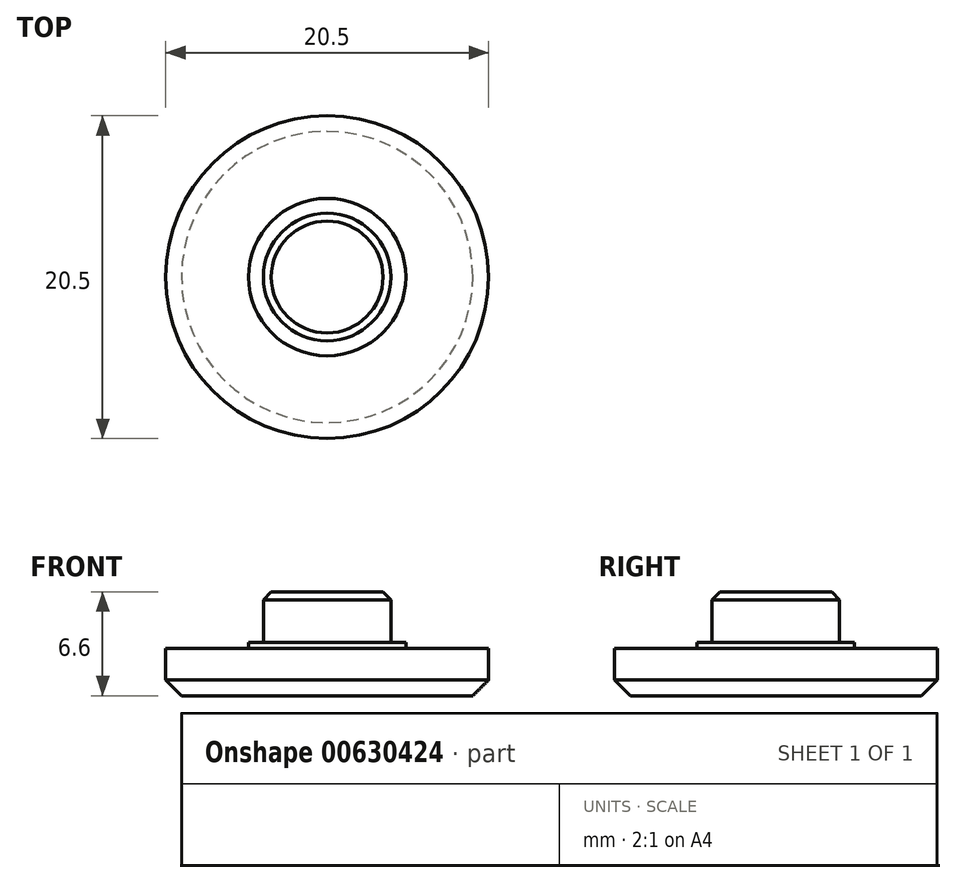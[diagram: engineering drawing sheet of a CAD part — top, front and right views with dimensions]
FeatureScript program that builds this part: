
annotation { "Feature Type Name" : "Feature", "Feature Type Description" : "" }
export const myFeature = defineFeature(function(context is Context, id is Id, definition is map)
    precondition{}
    {
        {
            var Q0;
            Q0=qCreatedBy(makeId("Top.planeOp"),FACE);
            var sketch = newSketch(context, id + "F0", { "sketchPlane" : qUnion([Q0])});
            skCircle(sketch, "E0", {"center": v(0, 0) * mm, "radius": 4.05 * mm});
            skCircle(sketch, "E1", {"center": v(0, 0) * mm, "radius": 10.25 * mm});
            skCircle(sketch, "E2", {"center": v(0, 0) * mm, "radius": 5 * mm});
            skSolve(sketch);
        }
        {
            assignVariable(context, id + "F1", {"name" : "CapThickness", "anyValue" : 3});
        }
        {
            assignVariable(context, id + "F2", {"name" : "Flange", "anyValue" : 0.4});
        }
        {
            assignVariable(context, id + "F3", {"name" : "Insert", "anyValue" : 3.2});
        }
        {
            var Q0;
            Q0=makeQuery(id+"F0.imprint","IMPRINT",FACE,{"disambiguationData":[TD([[makeQuery(id+"F0.imprint","IMPRINT",EDGE,{"derivedFrom":sQuery(id+"F0.wireOp",EDGE,"E1")}),1.0]])]});
            extrude(context, id + "F4", {"entities" : qUnion([Q0]), "depth" : (getVariable(context, 'CapThickness')) * mm, "offsetDistance" : 25 * mm});
        }
        {
            var Q0;
            Q0=makeQuery(id+"F0.imprint","IMPRINT",FACE,{"disambiguationData":[TD([[makeQuery(id+"F0.imprint","IMPRINT",EDGE,{"derivedFrom":sQuery(id+"F0.wireOp",EDGE,"E0")}),-1.0]])]});
            extrude(context, id + "F5", {"entities" : qUnion([Q0]), "operationType" : NewBodyOperationType.ADD, "depth" : (getVariable(context, 'CapThickness') + getVariable(context, 'Flange')) * mm, "offsetDistance" : 25 * mm});
        }
        {
            var Q0;
            Q0=makeQuery(id+"F0.imprint","IMPRINT",FACE,{"disambiguationData":[TD([[makeQuery(id+"F0.imprint","IMPRINT",EDGE,{"derivedFrom":sQuery(id+"F0.wireOp",EDGE,"E0")}),1.0]])]});
            extrude(context, id + "F6", {"entities" : qUnion([Q0]), "operationType" : NewBodyOperationType.ADD, "depth" : (getVariable(context, 'CapThickness') + getVariable(context, 'Flange') + getVariable(context, 'Insert')) * mm, "offsetDistance" : 25 * mm});
        }
        {
            var Q0;
            Q0=makeQuery(id+"F4.opExtrude","CAP_EDGE",EDGE,{"disambiguationData":[OSD([sQuery(id+"F0.wireOp",EDGE,"E1")])],"isStart":true});
            chamfer(context, id + "F7", {"entities" : qUnion([Q0]), "width" : 1 * mm, "tangentPropagation" : true});
        }
        {
            var Q0;
            Q0=makeQuery(id+"F6.opExtrude","CAP_EDGE",EDGE,{"disambiguationData":[OSD([sQuery(id+"F0.wireOp",EDGE,"E0")])],"isStart":false});
            chamfer(context, id + "F8", {"entities" : qUnion([Q0]), "width" : .5 * mm, "tangentPropagation" : true});
        }
    });
